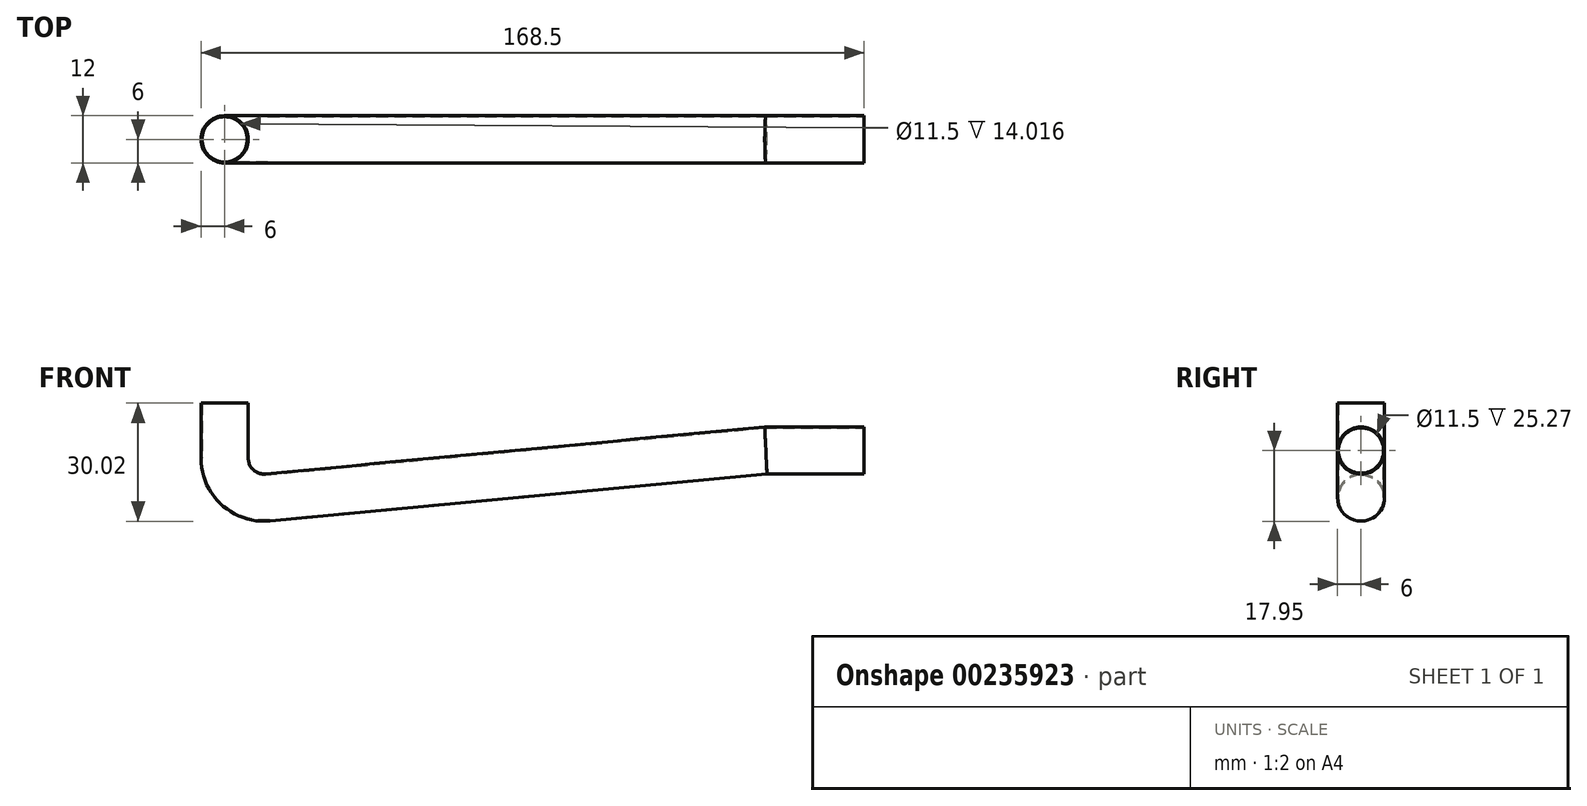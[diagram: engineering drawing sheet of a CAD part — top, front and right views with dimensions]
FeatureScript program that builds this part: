
annotation { "Feature Type Name" : "Feature", "Feature Type Description" : "" }
export const myFeature = defineFeature(function(context is Context, id is Id, definition is map)
    precondition{}
    {
        {
            var Q0;
            Q0=qCreatedBy(makeId("Front.planeOp"),FACE);
            var sketch = newSketch(context, id + "F0", { "sketchPlane" : qUnion([Q0])});
            skLineSegment(sketch, "E0", {"start": v(0, 0) * mm, "end": v(0, -25) * mm, "construction": true});
            skLineSegment(sketch, "E1", {"start": v(0, -25) * mm, "end": v(-6, -25) * mm, "construction": true});
            skLineSegment(sketch, "E2", {"start": v(0, 0) * mm, "end": v(-6, 0) * mm});
            skLineSegment(sketch, "E3", {"start": v(0, -25) * mm, "end": v(0, -12.07) * mm, "construction": true});
            skLineSegment(sketch, "E4", {"start": v(162.5, -12.07) * mm, "end": v(162.5, -12.04) * mm});
            skLineSegment(sketch, "E5", {"start": v(162.5, -12.04) * mm, "end": v(162.5, -12.07) * mm});
            skLineSegment(sketch, "E6", {"start": v(162.5, -12.07) * mm, "end": v(137.5, -12.07) * mm, "construction": true});
            skArc(sketch, "E7", {"start": v(137.5, -12.07) * mm, "mid": v(134.54, -11.62) * mm, "end": v(131.84, -10.31) * mm, "construction": true});
            skPoint(sketch, "E8.end.orphan", {"position": v(162.5, -25) * mm});
            skLineSegment(sketch, "E9", {"start": v(0, 0) * mm, "end": v(6, 0) * mm});
            skLineSegment(sketch, "E10", {"start": v(162.5, -12.07) * mm, "end": v(137.5, -12.07) * mm});
            skLineSegment(sketch, "E11", {"start": v(162.5, -18.04) * mm, "end": v(162.5, -25) * mm, "construction": true});
            skLineSegment(sketch, "E12", {"start": v(162.5, -25) * mm, "end": v(-23.61, -25) * mm, "construction": true});
            skLineSegment(sketch, "E13.0", {"start": v(0, 0) * mm, "end": v(0, -14.02) * mm});
            skLineSegment(sketch, "E14.0", {"start": v(137.5, -12.07) * mm, "end": v(10.94, -23.97) * mm});
            skArc(sketch, "E15.0", {"start": v(0, -14.02) * mm, "mid": v(3.27, -21.41) * mm, "end": v(10.94, -23.97) * mm});
            skSolve(sketch);
        }
        {
            var Q0;
            Q0=qCreatedBy(makeId("Top.planeOp"),FACE);
            var sketch = newSketch(context, id + "F1", { "sketchPlane" : qUnion([Q0])});
            skCircle(sketch, "E16", {"center": v(0, 0) * mm, "radius": 6 * mm});
            skCircle(sketch, "E17", {"center": v(0, 0) * mm, "radius": 5.75 * mm});
            skSolve(sketch);
        }
        {
            var Q0;
            Q0=makeQuery(id+"F1.imprint","IMPRINT",FACE,{"disambiguationData":[TD([[makeQuery(id+"F1.imprint","IMPRINT",EDGE,{"derivedFrom":sQuery(id+"F1.wireOp",EDGE,"E16")}),1.0]])]});
            var Q1;
            Q1=sQuery(id+"F1.wireOp",EDGE,"E16");
            var Q2;
            Q2=sQuery(id+"F1.wireOp",EDGE,"E17");
            var Q3;
            Q3=sQuery(id+"F0.wireOp",EDGE,"E13.0");
            var Q4;
            Q4=sQuery(id+"F0.wireOp",EDGE,"E15.0");
            var Q5;
            Q5=sQuery(id+"F0.wireOp",EDGE,"E14.0");
            var Q6;
            Q6=sQuery(id+"F0.wireOp",EDGE,"E10");
            sweep(context, id + "F2", {"profiles" : qUnion([Q0]), "surfaceProfiles" : qUnion([Q1, Q2]), "path" : qUnion([Q3, Q4, Q5, Q6])});
        }
    });
